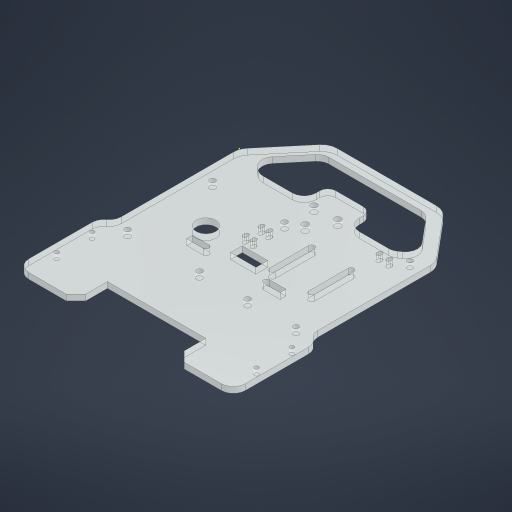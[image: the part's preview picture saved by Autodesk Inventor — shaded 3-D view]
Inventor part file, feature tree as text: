
AUTODESK INVENTOR PART (.ipt)
format: ipt  version: 2023 (Build 270158000, 158)  size: 454,656 bytes
history: native  units: mm
features: sketch x3, extrude x2, fillet x1, chamfer x1
ambient origin geometry x8: Origin, YZ Plane, XZ Plane, XY Plane, X Axis, Y Axis, Z Axis, Center Point
bodies: Solid1 (feature_tree)
feature tree (7):
  extrude  "Extrusion1"  Depth=100.0mm
  fillet  "Fillet1"  Radius=8.0mm
  sketch  "Sketch2"  dims[d4=2.2mm d5=18.0mm]
  extrude  "Extrusion2"  Depth=18.0mm
  chamfer  "Chamfer2"  Distance=36.576mm
  sketch  "Sketch1"  dims[d0=100.0mm d1=100.0mm d2=8.0mm]
  sketch  "Sketch3"  dims[d6=43.18mm d7=36.576mm d8=3.0mm d9=49.0mm d10=58.0mm d15=2.75mm d27=3.0mm d28=0.0mm d33=22.0mm d34=25.0mm d36=22.68928mm d37=6.0mm d38=6.0mm d39=12.0mm d40=6.0mm d41=8.0mm d44=2.3mm d45=13.462mm d46=5.0mm d47=14.0mm d48=15.5mm d49=3.3mm d54=4.0mm d55=5.0mm d56=34.0mm d57=4.25mm d58=6.0mm d59=30.0mm d60=8.0mm d61=8.0mm d62=30.0mm d64=360.0deg d66=3.0mm d67=18.0mm d68=20.0mm d69=20.0mm d71=20.0mm d72=10.0mm d74=10.0mm d76=1.0mm d77=2.0mm d78=4.0mm d79=20.0mm d81=5.0mm d82=10.0mm d84=10.0mm d86=1.0mm d87=2.0mm d88=20.0mm d90=4.0mm d91=10.0mm d93=10.0mm d95=20.0mm d97=8.0mm d98=10.0mm d100=10.0mm d102=27.0mm d103=3.0mm d104=0.0mm d105=5.0mm d106=2.0mm d107=45.0deg d108=10.0mm d109=3.0mm d110=47.5mm d111=3.0mm d113=11.0mm d114=2.0mm d115=13.0mm d116=6.9mm d117=6.0mm]
